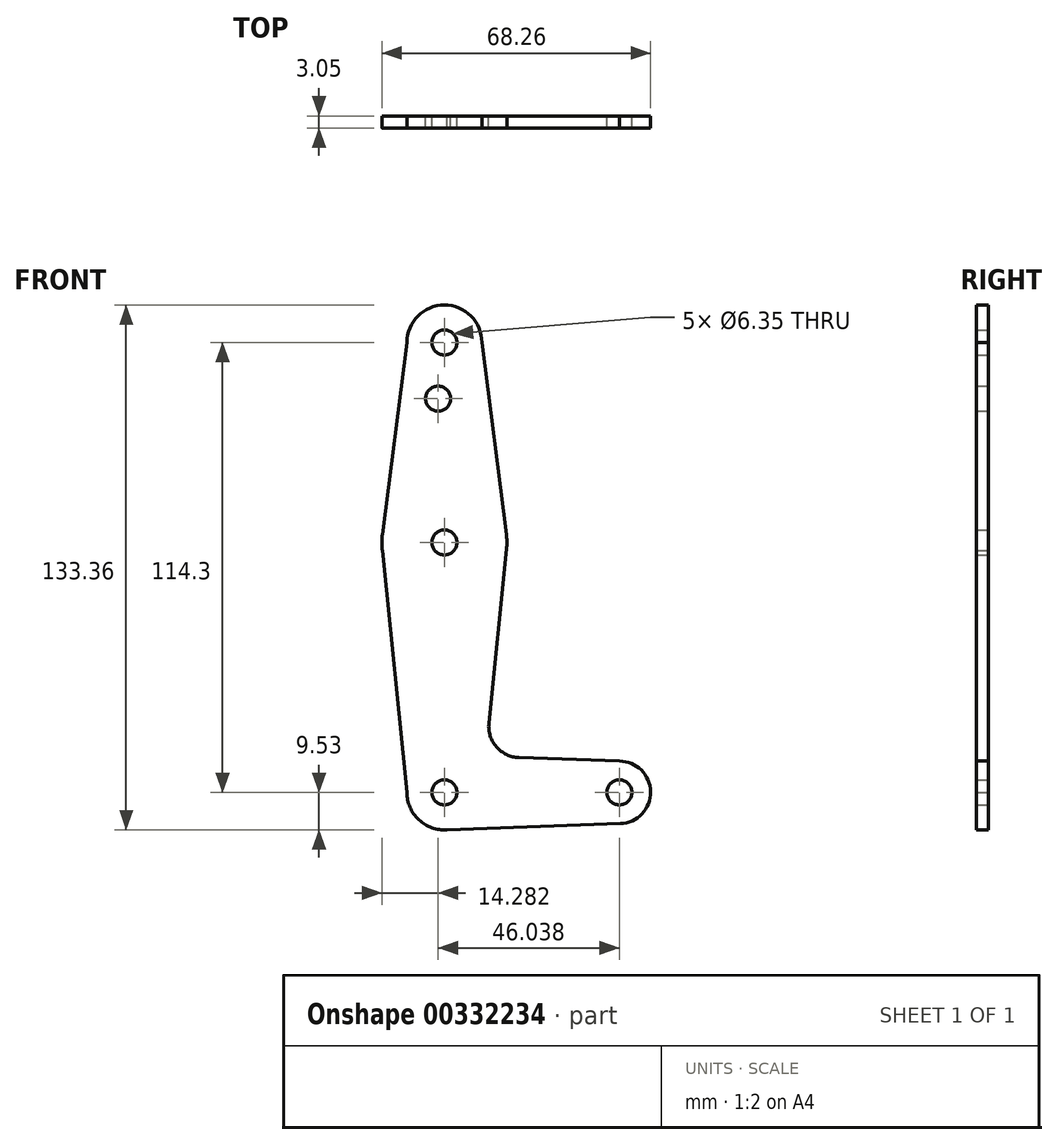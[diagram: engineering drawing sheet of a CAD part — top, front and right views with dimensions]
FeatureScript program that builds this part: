
annotation { "Feature Type Name" : "Feature", "Feature Type Description" : "" }
export const myFeature = defineFeature(function(context is Context, id is Id, definition is map)
    precondition{}
    {
        {
            var Q0;
            Q0=qCreatedBy(makeId("Front.planeOp"),FACE);
            var sketch = newSketch(context, id + "F0", { "sketchPlane" : qUnion([Q0])});
            skLineSegment(sketch, "E0", {"start": v(0, 0) * mm, "end": v(0, 114.3) * mm, "construction": true});
            skLineSegment(sketch, "E1", {"start": v(0, 0) * mm, "end": v(44.45, 0) * mm, "construction": true});
            skCircle(sketch, "E2", {"center": v(0, 114.3) * mm, "radius": 9.53 * mm});
            skCircle(sketch, "E3", {"center": v(0, 0) * mm, "radius": 9.53 * mm});
            skCircle(sketch, "E4", {"center": v(44.45, 0) * mm, "radius": 7.94 * mm});
            skCircle(sketch, "E5", {"center": v(0, 63.5) * mm, "radius": 15.88 * mm});
            skLineSegment(sketch, "E6", {"start": v(-9.53, 114.3) * mm, "end": v(-15.75, 65.5) * mm});
            skLineSegment(sketch, "E7", {"start": v(9.53, 114.3) * mm, "end": v(15.75, 65.5) * mm});
            skLineSegment(sketch, "E8", {"start": v(15.75, 65.5) * mm, "end": v(16, 63.5) * mm});
            skLineSegment(sketch, "E9", {"start": v(-9.53, 0) * mm, "end": v(-15.75, 61.5) * mm});
            skLineSegment(sketch, "E10", {"start": v(11.3, 17.6) * mm, "end": v(15.8, 61.9) * mm});
            skLineSegment(sketch, "E11", {"start": v(18.93, 8.85) * mm, "end": v(44.45, 7.94) * mm});
            skLineSegment(sketch, "E12", {"start": v(0, -9.53) * mm, "end": v(44.73, -7.93) * mm});
            skCircle(sketch, "E13", {"center": v(0, 114.3) * mm, "radius": 3.18 * mm});
            skCircle(sketch, "E14", {"center": v(0, 0) * mm, "radius": 3.18 * mm});
            skCircle(sketch, "E15", {"center": v(-1.59, 100.03) * mm, "radius": 3.18 * mm});
            skArc(sketch, "E16.filletArc", {"start": v(11.3, 17.6) * mm, "mid": v(13.22, 11.57) * mm, "end": v(18.93, 8.85) * mm});
            skCircle(sketch, "E17", {"center": v(0, 63.5) * mm, "radius": 3.18 * mm});
            skCircle(sketch, "E18", {"center": v(44.45, 0) * mm, "radius": 3.18 * mm});
            skSolve(sketch);
        }
        {
            var Q0;
            Q0 = qSketchRegion(id + "F0", true);
            extrude(context, id + "F1", {"entities" : qUnion([Q0]), "depth" : 3.05 * mm});
        }
    });
